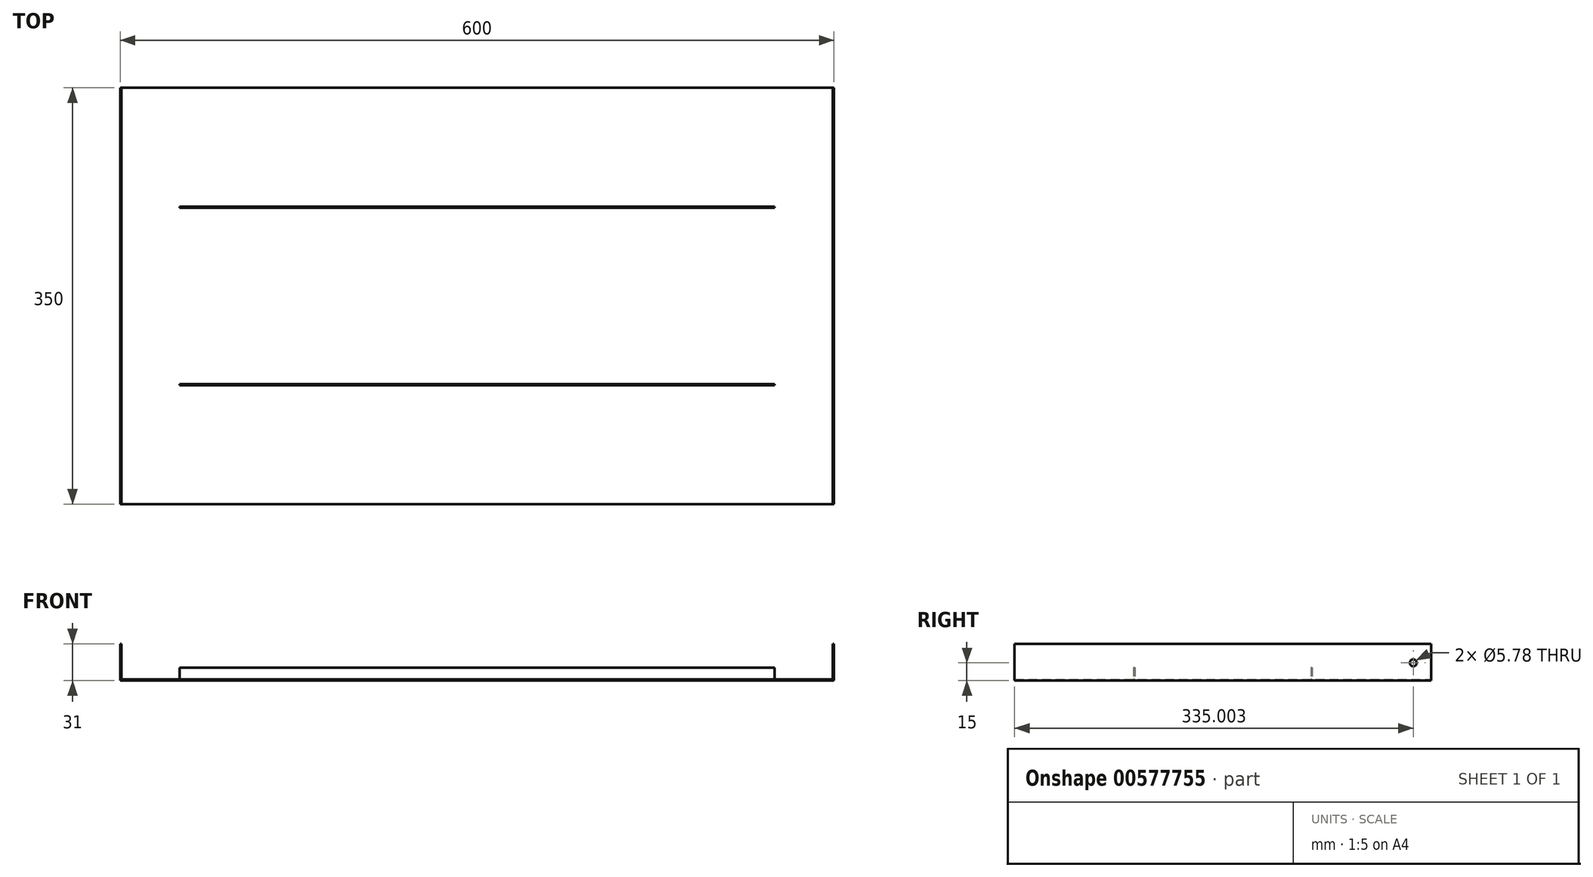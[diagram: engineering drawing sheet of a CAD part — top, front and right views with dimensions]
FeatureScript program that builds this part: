
annotation { "Feature Type Name" : "Feature", "Feature Type Description" : "" }
export const myFeature = defineFeature(function(context is Context, id is Id, definition is map)
    precondition{}
    {
        {
            var Q0;
            Q0=qCreatedBy(makeId("Top.planeOp"),FACE);
            var sketch = newSketch(context, id + "F0", { "sketchPlane" : qUnion([Q0])});
            skLineSegment(sketch, "E0.bottom", {"start": v(-296.52, 177.82) * mm, "end": v(303.48, 177.82) * mm});
            skLineSegment(sketch, "E0.top", {"start": v(-296.52, -172.18) * mm, "end": v(303.48, -172.18) * mm});
            skLineSegment(sketch, "E0.left", {"start": v(-296.52, 177.82) * mm, "end": v(-296.52, -172.18) * mm});
            skLineSegment(sketch, "E0.right", {"start": v(303.48, 177.82) * mm, "end": v(303.48, -172.18) * mm});
            skSolve(sketch);
        }
        {
            var Q0;
            Q0=makeQuery(id+"F0.imprint","IMPRINT",FACE,{"disambiguationData":[TD([[makeQuery(id+"F0.imprint","IMPRINT",EDGE,{"derivedFrom":sQuery(id+"F0.wireOp",EDGE,"E0.bottom")}),-1.0]])]});
            extrude(context, id + "F1", {"entities" : qUnion([Q0]), "depth" : 1 * mm, "offsetDistance" : 25 * mm});
        }
        {
            var Q0;
            Q0=makeQuery(id+"F1.opExtrude","CAP_FACE",FACE,{"disambiguationData":[OSD([sQuery(id+"F0.wireOp",EDGE,"E0.bottom"),sQuery(id+"F0.wireOp",EDGE,"E0.top"),sQuery(id+"F0.wireOp",EDGE,"E0.left"),sQuery(id+"F0.wireOp",EDGE,"E0.right")])],"isStart":false});
            var sketch = newSketch(context, id + "F2", { "sketchPlane" : qUnion([Q0])});
            skLineSegment(sketch, "E1.bottom", {"start": v(-296.52, 177.82) * mm, "end": v(-295.52, 177.82) * mm});
            skLineSegment(sketch, "E1.top", {"start": v(-296.52, -172.18) * mm, "end": v(-295.52, -172.18) * mm});
            skLineSegment(sketch, "E1.left", {"start": v(-296.52, 177.82) * mm, "end": v(-296.52, -172.18) * mm});
            skLineSegment(sketch, "E1.right", {"start": v(-295.52, 177.82) * mm, "end": v(-295.52, -172.18) * mm});
            skLineSegment(sketch, "E2.bottom", {"start": v(303.48, -172.18) * mm, "end": v(302.48, -172.18) * mm});
            skLineSegment(sketch, "E2.top", {"start": v(303.48, 177.82) * mm, "end": v(302.48, 177.82) * mm});
            skLineSegment(sketch, "E2.left", {"start": v(303.48, -172.18) * mm, "end": v(303.48, 177.82) * mm});
            skLineSegment(sketch, "E2.right", {"start": v(302.48, -172.18) * mm, "end": v(302.48, 177.82) * mm});
            skSolve(sketch);
        }
        {
            var Q0;
            Q0 = qSketchRegion(id + "F2", true);
            extrude(context, id + "F3", {"entities" : qUnion([Q0]), "operationType" : NewBodyOperationType.ADD, "depth" : 30 * mm, "offsetDistance" : 25 * mm});
        }
        {
            var Q0;
            Q0=makeQuery(id+"F3.boolean.opBoolean","MERGE",FACE,{"derivedFrom":[makeQuery(id+"F1.opExtrude","SWEPT_FACE",FACE,{"disambiguationData":[OSD([sQuery(id+"F0.wireOp",EDGE,"E0.left")])]}),makeQuery(id+"F3.opExtrude","SWEPT_FACE",FACE,{"disambiguationData":[OSD([sQuery(id+"F2.wireOp",EDGE,"E1.left")])]})]});
            var sketch = newSketch(context, id + "F4", { "sketchPlane" : qUnion([Q0])});
            skCircle(sketch, "E3", {"center": v(-162.82, 15) * mm, "radius": 2.89 * mm});
            skSolve(sketch);
        }
        {
            var Q0;
            Q0 = qSketchRegion(id + "F4", true);
            extrude(context, id + "F5", {"entities" : qUnion([Q0]), "operationType" : NewBodyOperationType.REMOVE, "oppositeDirection" : true, "depth" : 735 * mm, "offsetDistance" : 25 * mm});
        }
        {
            var Q0;
            Q0=makeQuery(id+"F1.opExtrude","CAP_FACE",FACE,{"disambiguationData":[OSD([sQuery(id+"F0.wireOp",EDGE,"E0.bottom"),sQuery(id+"F0.wireOp",EDGE,"E0.top"),sQuery(id+"F0.wireOp",EDGE,"E0.left"),sQuery(id+"F0.wireOp",EDGE,"E0.right")])],"isStart":false});
            var sketch = newSketch(context, id + "F6", { "sketchPlane" : qUnion([Q0])});
            skLineSegment(sketch, "E4.bottom", {"start": v(-246.52, 77.82) * mm, "end": v(253.48, 77.82) * mm});
            skLineSegment(sketch, "E4.top", {"start": v(-246.52, 76.82) * mm, "end": v(253.48, 76.82) * mm});
            skLineSegment(sketch, "E4.left", {"start": v(-246.52, 77.82) * mm, "end": v(-246.52, 76.82) * mm});
            skLineSegment(sketch, "E4.right", {"start": v(253.48, 77.82) * mm, "end": v(253.48, 76.82) * mm});
            skLineSegment(sketch, "E5.bottom", {"start": v(-246.52, -71.18) * mm, "end": v(253.48, -71.18) * mm});
            skLineSegment(sketch, "E5.top", {"start": v(-246.52, -72.18) * mm, "end": v(253.48, -72.18) * mm});
            skLineSegment(sketch, "E5.left", {"start": v(-246.52, -71.18) * mm, "end": v(-246.52, -72.18) * mm});
            skLineSegment(sketch, "E5.right", {"start": v(253.48, -71.18) * mm, "end": v(253.48, -72.18) * mm});
            skSolve(sketch);
        }
        {
            var Q0;
            Q0 = qSketchRegion(id + "F6", true);
            extrude(context, id + "F7", {"entities" : qUnion([Q0]), "operationType" : NewBodyOperationType.ADD, "depth" : 10 * mm, "offsetDistance" : 25 * mm});
        }
    });
